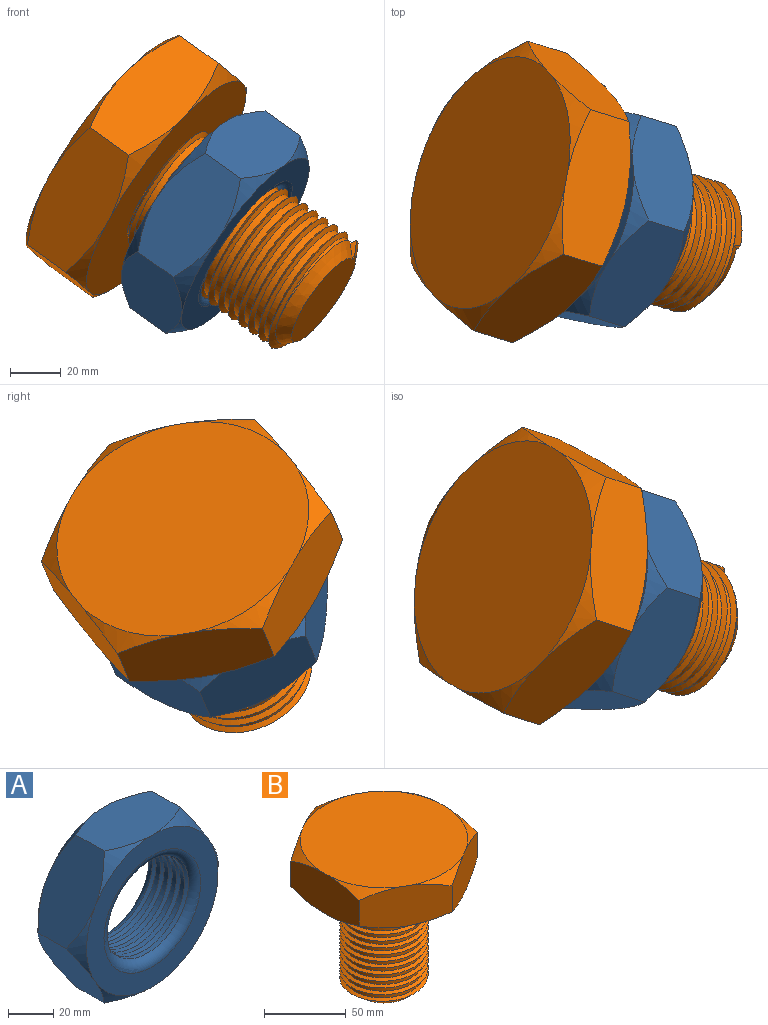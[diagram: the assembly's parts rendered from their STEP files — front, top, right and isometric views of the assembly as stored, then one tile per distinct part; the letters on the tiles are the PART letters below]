
ASSEMBLY  parts=2 mates=1
PART A: 26 faces, bbox 94.6x30.7x94.5 mm
  f0: plane 81.86x81.86mm, normal (0,-1,0), area 2420.5mm2, adj f9,f20,f21,f22,f23,f24,f25
  f1: plane 47.28x30.02mm, normal (0,0,1), area 1221.6mm2, adj f2,f6,f7,f16,f17,f21,f25
  f2: plane 40.96x30.04mm, normal (-0.87,0,0.5), area 1221.6mm2, adj f1,f3,f7,f17,f18,f24,f25
  f3: plane 40.96x30.04mm, normal (-0.87,0,-0.5), area 1221.6mm2, adj f2,f4,f7,f18,f19,f23,f24
  f4: plane 47.28x30.02mm, normal (0,0,-1), area 1221.6mm2, adj f3,f5,f7,f14,f19,f22,f23
  f5: plane 40.96x30.04mm, normal (0.87,0,-0.5), area 1221.6mm2, adj f4,f6,f7,f14,f15,f20,f22
  f6: plane 40.96x30.04mm, normal (0.87,0,0.5), area 1221.6mm2, adj f1,f5,f7,f15,f16,f20,f21
  f7: plane 82.3x81.86mm, normal (0,1,0), area 2469.2mm2, adj f1,f2,f3,f4,f5,f6,f10,f14
  f8: cylinder r=25mm len=50mm, axis (0,1,0), area 1708.7mm2, adj f9,f10,f12,f13
  f9: torus R=30.08mm, axis (0,-1,0), area 1164.1mm2, adj f0,f8,f12,f13
  f10: torus R=30.08mm, axis (0,-1,0), area 1114.8mm2, adj f7,f8,f11,f12,f13
  f11: plane 0.58x0.41mm, normal (0,0,1), area 0mm2, adj f10,f12,f13
  f12: bspline ~62.45x54.09mm, area 1969.5mm2, adj f8,f9,f10,f11,f13
  f13: bspline ~62.45x54.09mm, area 1974.6mm2, adj f8,f9,f10,f11,f12
  f14: cone r=53.51mm half-angle=45deg, axis (0,-1,0), area 115.9mm2, adj f4,f5,f7
  f15: cone r=53.51mm half-angle=45deg, axis (0,-1,0), area 115.9mm2, adj f5,f6,f7
  f16: cone r=53.51mm half-angle=45deg, axis (0,-1,0), area 115.9mm2, adj f1,f6,f7
  f17: cone r=53.51mm half-angle=45deg, axis (0,-1,0), area 115.9mm2, adj f1,f2,f7
  f18: cone r=53.51mm half-angle=45deg, axis (0,-1,0), area 115.9mm2, adj f2,f3,f7
  f19: cone r=53.51mm half-angle=45deg, axis (0,-1,0), area 115.9mm2, adj f3,f4,f7
  f20: cone r=53.51mm half-angle=45deg, axis (0,1,0), area 127.3mm2, adj f0,f5,f6
  f21: cone r=53.51mm half-angle=45deg, axis (0,1,0), area 127.3mm2, adj f0,f1,f6
  f22: cone r=53.51mm half-angle=45deg, axis (0,1,0), area 127.3mm2, adj f0,f4,f5
  f23: cone r=53.51mm half-angle=45deg, axis (0,1,0), area 127.3mm2, adj f0,f3,f4
  f24: cone r=53.51mm half-angle=45deg, axis (0,1,0), area 127.3mm2, adj f0,f2,f3
  f25: cone r=53.51mm half-angle=45deg, axis (0,1,0), area 127.3mm2, adj f0,f1,f2
PART B: 26 faces, bbox 121.6x121.9x114.5 mm
  f0: plane 55.07x34.06mm, normal (-0.5,-0.87,0), area 1556.3mm2, adj f1,f5,f6,f7,f17,f18,f21,f22
  f1: plane 55.07x34.06mm, normal (0.5,-0.87,0), area 1556.3mm2, adj f0,f2,f6,f7,f18,f19,f20,f21
  f2: plane 62.98x34.07mm, normal (1,0,0), area 1556.3mm2, adj f1,f3,f6,f7,f14,f19,f20,f25
  f3: plane 55.07x34.06mm, normal (0.5,0.87,0), area 1556.3mm2, adj f2,f4,f6,f7,f14,f15,f24,f25
  f4: plane 55.07x34.06mm, normal (-0.5,0.87,0), area 1556.3mm2, adj f3,f5,f6,f7,f15,f16,f23,f24
  f5: plane 62.98x34.07mm, normal (-1,0,0), area 1556.3mm2, adj f0,f4,f6,f7,f16,f17,f22,f23
  f6: plane 102.42x102.03mm, normal (0,0,1), area 8232.1mm2, adj f0,f1,f2,f3,f4,f5,f20,f21
  f7: plane 103.3x103.1mm, normal (0,0,-1), area 6163mm2, adj f0,f1,f2,f3,f4,f5,f8,f9
  f8: cylinder r=25mm len=73.12mm, axis (0,0,1), area 6749.2mm2, adj f7,f9,f10,f13
  f9: bspline ~77.29x62.45mm, area 5730.9mm2, adj f7,f8,f10,f11,f13
  f10: bspline ~82.09x62.45mm, area 6117.9mm2, adj f7,f8,f9,f11,f12,f13
  f11: plane 7.12x4.62mm, normal (0,-1,0), area 11.7mm2, adj f9,f10,f12,f13
  f12: plane 42.21x40.59mm, normal (0,0,-1), area 1266mm2, adj f10,f11,f13
  f13: cone r=19.92mm half-angle=45deg, axis (0,0,1), area 606mm2, adj f8,f9,f10,f11,f12
  f14: cone r=64.84mm half-angle=55.2deg, axis (0,0,1), area 235.4mm2, adj f2,f3,f7
  f15: cone r=64.84mm half-angle=55.2deg, axis (0,0,1), area 235.4mm2, adj f3,f4,f7
  f16: cone r=64.84mm half-angle=55.2deg, axis (0,0,1), area 235.4mm2, adj f4,f5,f7
  f17: cone r=64.84mm half-angle=55.2deg, axis (0,0,1), area 235.4mm2, adj f0,f5,f7
  f18: cone r=64.84mm half-angle=55.2deg, axis (0,0,1), area 235.4mm2, adj f0,f1,f7
  f19: cone r=64.84mm half-angle=55.2deg, axis (0,0,1), area 235.4mm2, adj f1,f2,f7
  f20: cone r=64.84mm half-angle=55.2deg, axis (0,0,-1), area 219.6mm2, adj f1,f2,f6
  f21: cone r=64.84mm half-angle=55.2deg, axis (0,0,-1), area 219.6mm2, adj f0,f1,f6
  f22: cone r=64.84mm half-angle=55.2deg, axis (0,0,-1), area 219.6mm2, adj f0,f5,f6
  f23: cone r=64.84mm half-angle=55.2deg, axis (0,0,-1), area 219.6mm2, adj f4,f5,f6
  f24: cone r=64.84mm half-angle=55.2deg, axis (0,0,-1), area 219.6mm2, adj f3,f4,f6
  f25: cone r=64.84mm half-angle=55.2deg, axis (0,0,-1), area 219.6mm2, adj f2,f3,f6
PLACE A rot(axis=(0.77,-0.54,0.35),93.7deg) t=(-178.98,93.47,-209.99)mm fixed
PLACE B rot(axis=(-0.25,-0.96,-0.09),55.8deg) t=(-186.54,95.63,-204.91)mm
MATE cylindrical B.f12 <-> A.f8  axis (0.79,-0.24,-0.57) through (-124.71,76.73,-248.91)mm
